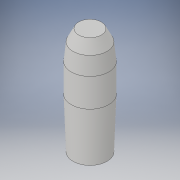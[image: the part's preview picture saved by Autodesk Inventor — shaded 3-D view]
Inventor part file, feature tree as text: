
AUTODESK INVENTOR PART (.ipt)
format: ipt  version: 2019 (Build 230136000, 136)  size: 121,856 bytes
history: native  units: in
note: dims shown in document units (in); Inventor stores cm internally (conversion verified against a paired STEP export)
features: sketch x4, plane x3, loft x3, other x3, extrude x1
ambient origin geometry x8: Origin, YZ Plane, XZ Plane, XY Plane, X Axis, Y Axis, Z Axis, Center Point
bodies: Solid1 (feature_tree)
feature tree (14):
  extrude  "Extrusion1"  Depth=0.9843in TaperAngle=0.0deg
  plane  "Work Plane1"
  loft  "Loft1"
  plane  "Work Plane2"
  loft  "Loft2"
  plane  "Work Plane3"
  loft  "Loft3"
  sketch  "Sketch1"  dims[d0=1.2992in d1=0.9843in d2=0.0in]
  sketch  "Sketch2"  dims[d3=1.7323in d4=1.1811in]
  other  "Edges1"
  sketch  "Sketch3"  dims[d5=0.0in d6=90.0deg d7=0.0in d8=90.0deg]
  other  "Edges2"
  sketch  "Sketch4"  dims[d9=0.5906in d10=1.1811in d11=0.0in d12=90.0deg d13=0.0in d14=90.0deg d15=0.3937in d16=0.7874in d17=0.0in d18=90.0deg d19=0.0in d20=90.0deg]
  other  "Edges3"
